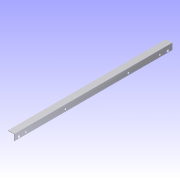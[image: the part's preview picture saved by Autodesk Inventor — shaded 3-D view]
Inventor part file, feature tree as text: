
AUTODESK INVENTOR PART (.ipt)
format: ipt  version: 2012 (Build 160160000, 160)  size: 94,720 bytes
history: native  units: in
note: dims shown in document units (in); Inventor stores cm internally (conversion verified against a paired STEP export)
features: extrude x2, sketch x2
ambient origin geometry x8: Origin, YZ Plane, XZ Plane, XY Plane, X Axis, Y Axis, Z Axis, Center Point
bodies: Solid1 (feature_tree)
feature tree (4):
  extrude  "Extrusion1"  Depth=2.0in
  extrude  "Extrusion2"  Depth=0.125in
  sketch  "Sketch1"  dims[d0=2.0in d1=2.0in]
  sketch  "Sketch2"  dims[d2=0.125in d3=0.125in d4=50.1875in d5=0.0in d8=0.8125in d9=0.5625in d12=1.5in d14=0.5625in d15=0.5625in d16=0.5625in d17=0.5625in d23=71.375in d24=0.0in d25=0.8125in d26=1.5in d27=1.5in d28=3.6875in d29=16.25in d30=36.25in d31=46.25in d33=48.75in d34=1.3125in]
